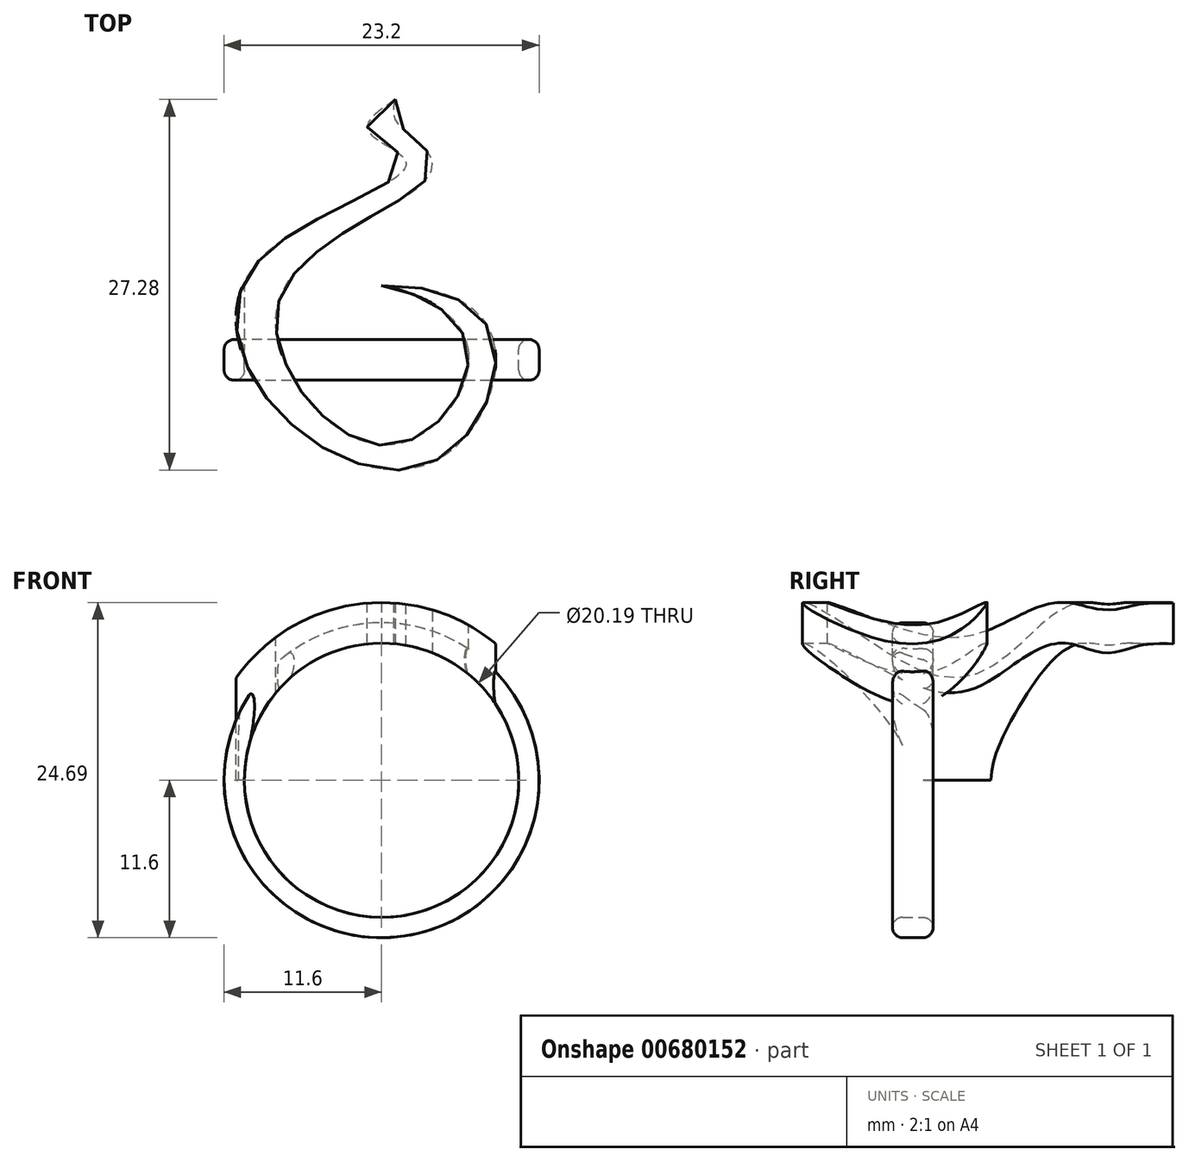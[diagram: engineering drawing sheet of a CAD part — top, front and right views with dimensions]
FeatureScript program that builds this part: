
annotation { "Feature Type Name" : "Feature", "Feature Type Description" : "" }
export const myFeature = defineFeature(function(context is Context, id is Id, definition is map)
    precondition{}
    {
        {
            var Q0;
            Q0=qCreatedBy(makeId("Front.planeOp"),FACE);
            var sketch = newSketch(context, id + "F0", { "sketchPlane" : qUnion([Q0])});
            skCircle(sketch, "E0", {"center": v(0, 0) * mm, "radius": 10.1 * mm});
            skCircle(sketch, "E1", {"center": v(0, 0) * mm, "radius": 11.6 * mm});
            skSolve(sketch);
        }
        {
            var Q0;
            Q0 = qSketchRegion(id + "F0", true);
            extrude(context, id + "F1", {"entities" : qUnion([Q0]), "depth" : 3 * mm, "offsetDistance" : 25.4 * mm});
        }
        {
            var Q0;
            Q0=makeQuery(id+"F1.opExtrude","CAP_EDGE",EDGE,{"disambiguationData":[OSD([sQuery(id+"F0.wireOp",EDGE,"E1")])],"isStart":false});
            var Q1;
            Q1=makeQuery(id+"F1.opExtrude","CAP_EDGE",EDGE,{"disambiguationData":[OSD([sQuery(id+"F0.wireOp",EDGE,"E0")])],"isStart":false});
            var Q2;
            Q2=makeQuery(id+"F1.opExtrude","CAP_EDGE",EDGE,{"disambiguationData":[OSD([sQuery(id+"F0.wireOp",EDGE,"E0")])],"isStart":true});
            var Q3;
            Q3=makeQuery(id+"F1.opExtrude","CAP_EDGE",EDGE,{"disambiguationData":[OSD([sQuery(id+"F0.wireOp",EDGE,"E1")])],"isStart":true});
            fillet(context, id + "F2", {"entities" : qUnion([Q0, Q1, Q2, Q3]), "radius" : 0.75 * mm, "tangentPropagation" : true, "allowEdgeOverflow" : false});
        }
        {
            var Q0;
            Q0=qCreatedBy(makeId("Top.planeOp"),FACE);
            var sketch = newSketch(context, id + "F3", { "sketchPlane" : qUnion([Q0])});
            skFitSpline(sketch, "E2", {"points": [v(0, 3.97) * mm, v(6.4, -1.43) * mm, v(0, -7.77) * mm, v(-7.69, 2.37) * mm, v(2.26, 10.88) * mm, v(3.68, 13.29) * mm, v(1.7, 15.4) * mm, v(0.99, 17.67) * mm], "startDerivative": vector(70.38, -13.27) * mm, "endDerivative": vector(9.94, 46.61) * mm});
            skFitSpline(sketch, "E3", {"points": [v(0.99, 17.67) * mm, v(-0.99, 15.36) * mm, v(1.81, 12.96) * mm, v(-8.98, 5.87) * mm, v(-8.29, -4.53) * mm, v(3, -9.33) * mm, v(8.4, -1.43) * mm, v(0, 3.97) * mm], "startDerivative": vector(-40.66, -27.53) * mm, "endDerivative": vector(-113.52, -1.92) * mm});
            skSolve(sketch);
        }
        {
            var Q0;
            Q0 = qSketchRegion(id + "F3", true);
            extrude(context, id + "F4", {"entities" : qUnion([Q0]), "operationType" : NewBodyOperationType.ADD, "depth" : 19.05 * mm, "offsetDistance" : 25.4 * mm});
        }
        {
            var Q0;
            Q0=makeQuery(id+"F0.imprint","IMPRINT",FACE,{"disambiguationData":[TD([[makeQuery(id+"F0.imprint","IMPRINT",EDGE,{"derivedFrom":sQuery(id+"F0.wireOp",EDGE,"E0")}),1.0]])]});
            extrude(context, id + "F5", {"entities" : qUnion([Q0]), "operationType" : NewBodyOperationType.REMOVE, "endBound" : BoundingType.SYMMETRIC, "oppositeDirection" : true, "depth" : 50.8 * mm, "offsetDistance" : 25.4 * mm});
        }
        {
            var Q0;
            Q0=qCreatedBy(makeId("Front.planeOp"),FACE);
            var sketch = newSketch(context, id + "F6", { "sketchPlane" : qUnion([Q0])});
            skCircle(sketch, "E4", {"center": v(0, 0) * mm, "radius": 13.1 * mm});
            skCircle(sketch, "E5", {"center": v(0, 0) * mm, "radius": 25.4 * mm});
            skSolve(sketch);
        }
        {
            var Q0;
            Q0 = qSketchRegion(id + "F6", true);
            extrude(context, id + "F7", {"entities" : qUnion([Q0]), "operationType" : NewBodyOperationType.REMOVE, "endBound" : BoundingType.SYMMETRIC, "oppositeDirection" : true, "depth" : 50.8 * mm, "offsetDistance" : 25.4 * mm});
        }
    });
